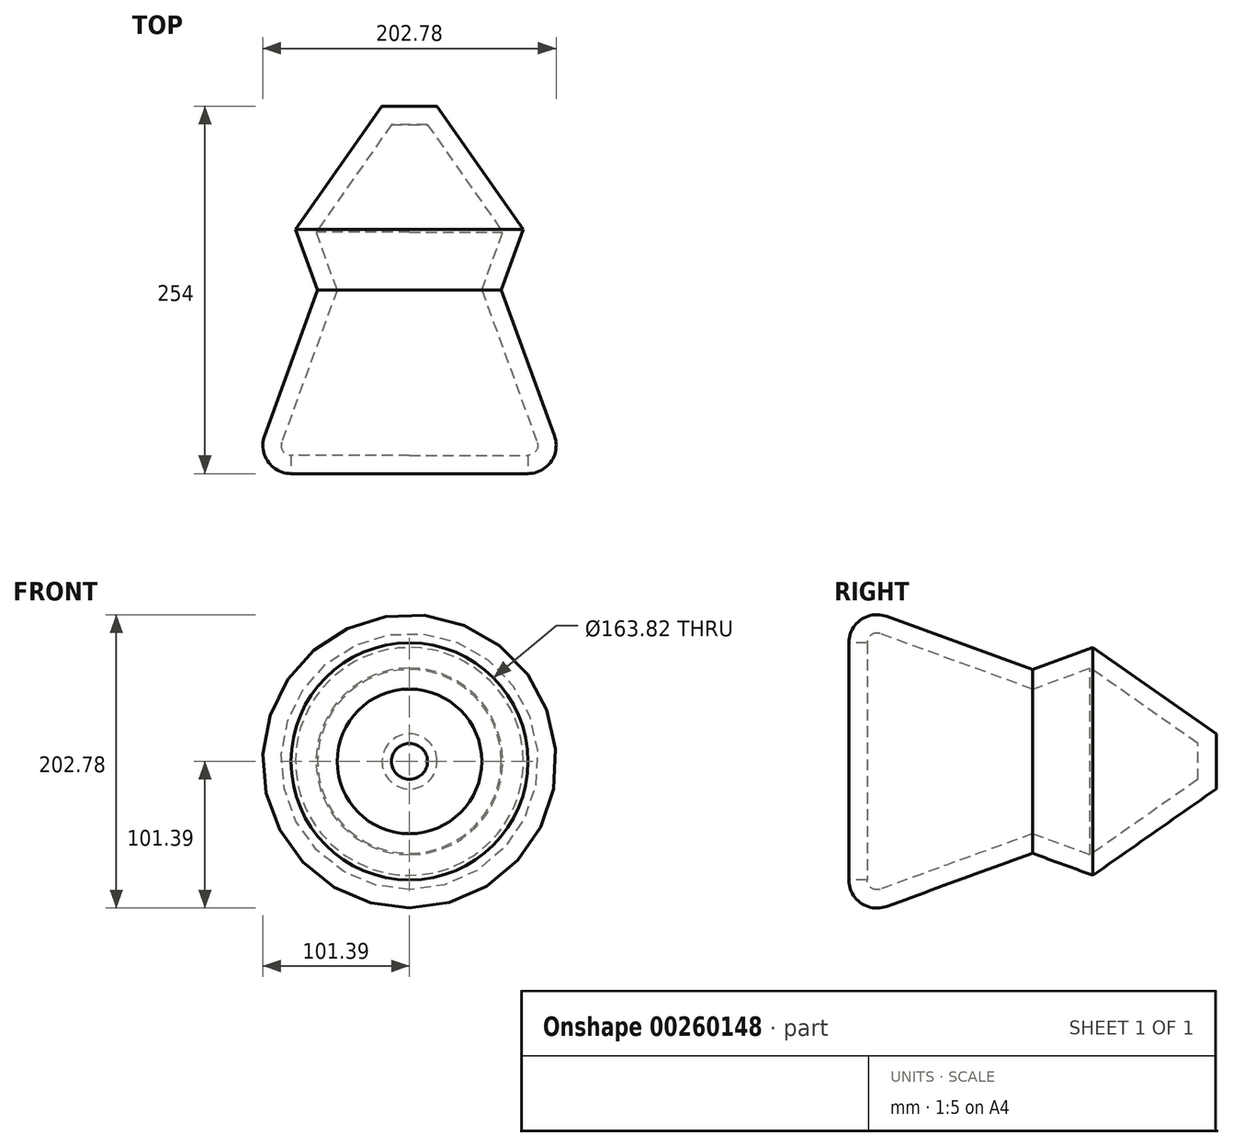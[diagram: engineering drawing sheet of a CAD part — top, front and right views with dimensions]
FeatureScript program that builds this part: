
annotation { "Feature Type Name" : "Feature", "Feature Type Description" : "" }
export const myFeature = defineFeature(function(context is Context, id is Id, definition is map)
    precondition{}
    {
        {
            var Q0;
            Q0=qCreatedBy(makeId("Front.planeOp"),FACE);
            var sketch = newSketch(context, id + "F0", { "sketchPlane" : qUnion([Q0])});
            skCircle(sketch, "E0", {"center": v(0, 0) * mm, "radius": 63.5 * mm});
            skSolve(sketch);
        }
        {
            var Q0;
            Q0=makeQuery(id+"F0.imprint","IMPRINT",FACE,{"disambiguationData":[TD([[makeQuery(id+"F0.imprint","IMPRINT",EDGE,{"derivedFrom":sQuery(id+"F0.wireOp",EDGE,"E0")}),1.0]])]});
            extrude(context, id + "F1", {"entities" : qUnion([Q0]), "endBound" : BoundingType.SYMMETRIC, "depth" : 254 * mm, "hasDraft" : true, "draftAngle" : 20 * degree});
        }
        {
            var Q0;
            Q0=makeQuery(id+"F1.opExtrude","CAP_EDGE",EDGE,{"disambiguationData":[OSD([sQuery(id+"F0.wireOp",EDGE,"E0")])],"isStart":false});
            fillet(context, id + "F2", {"entities" : qUnion([Q0]), "radius" : 19.47 * mm, "tangentPropagation" : true, "allowEdgeOverflow" : false});
        }
        {
            var Q0;
            Q0=makeQuery(id+"F1.opExtrude","CAP_FACE",FACE,{"disambiguationData":[OSD([sQuery(id+"F0.wireOp",EDGE,"E0")])],"isStart":true});
            chamfer(context, id + "F3", {"entities" : qUnion([Q0]), "width" : 63.5 * mm, "tangentPropagation" : true});
        }
        {
            var Q0;
            Q0=makeQuery(id+"F1.opExtrude","CAP_FACE",FACE,{"disambiguationData":[OSD([sQuery(id+"F0.wireOp",EDGE,"E0")])],"isStart":false});
            shell(context, id + "F4", {"entities" : qUnion([Q0]), "thickness" : 12.7 * mm});
        }
    });
